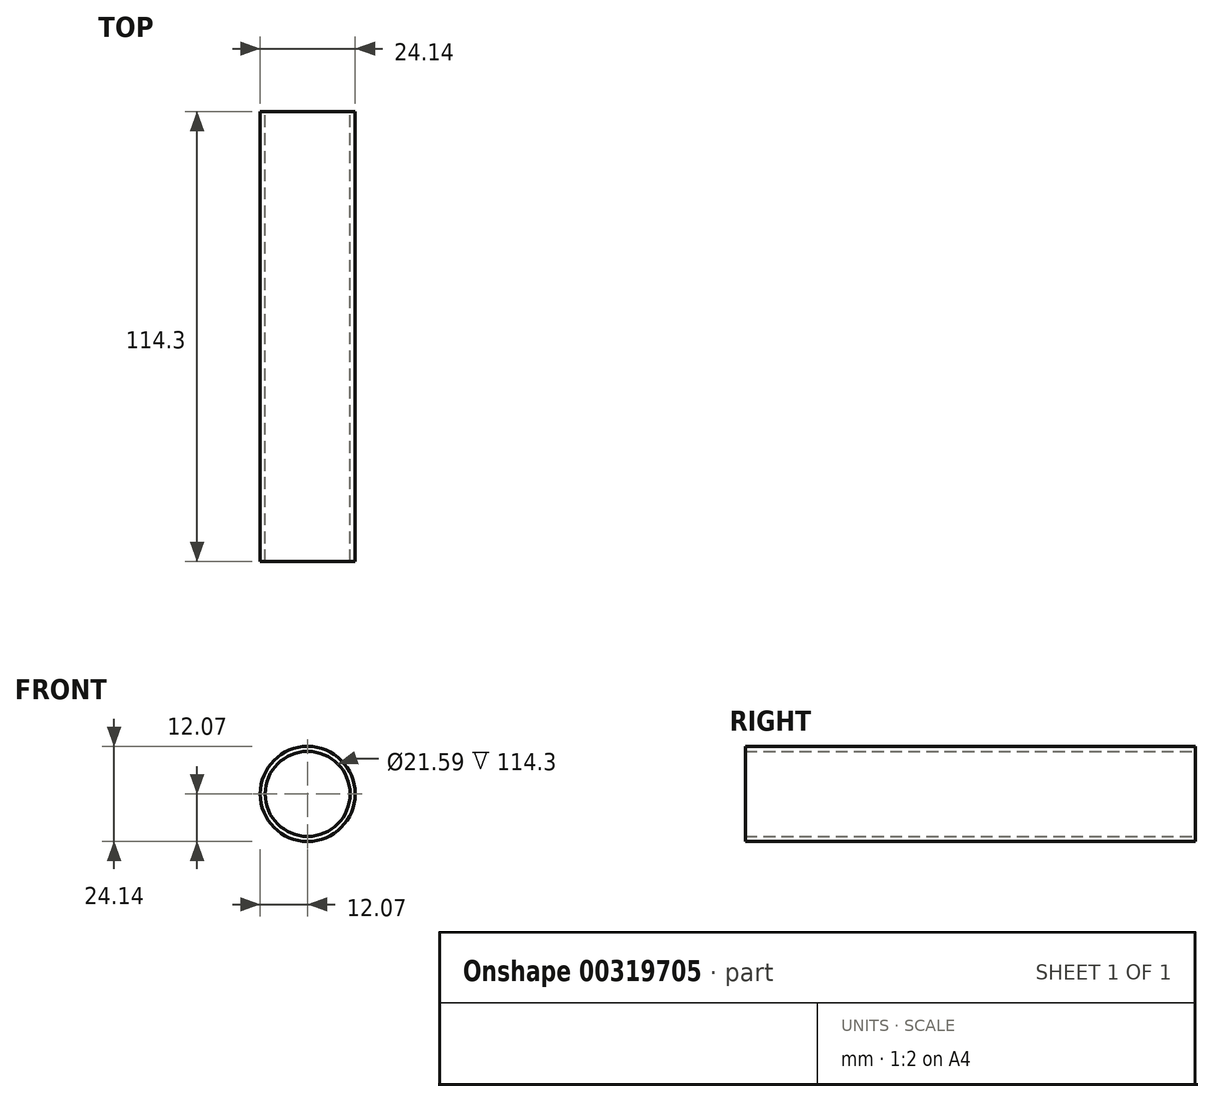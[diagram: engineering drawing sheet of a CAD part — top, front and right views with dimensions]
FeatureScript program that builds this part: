
annotation { "Feature Type Name" : "Feature", "Feature Type Description" : "" }
export const myFeature = defineFeature(function(context is Context, id is Id, definition is map)
    precondition{}
    {
        {
            var Q0;
            Q0=qCreatedBy(makeId("Front.planeOp"),FACE);
            var sketch = newSketch(context, id + "F0", { "sketchPlane" : qUnion([Q0])});
            skCircle(sketch, "E0", {"center": v(0, 0) * mm, "radius": 10.8 * mm});
            skCircle(sketch, "E1", {"center": v(0, 0) * mm, "radius": 12.07 * mm});
            skSolve(sketch);
        }
        {
            var Q0;
            Q0 = qSketchRegion(id + "F0", true);
            extrude(context, id + "F1", {"entities" : qUnion([Q0]), "depth" : 114.3 * mm});
        }
    });
